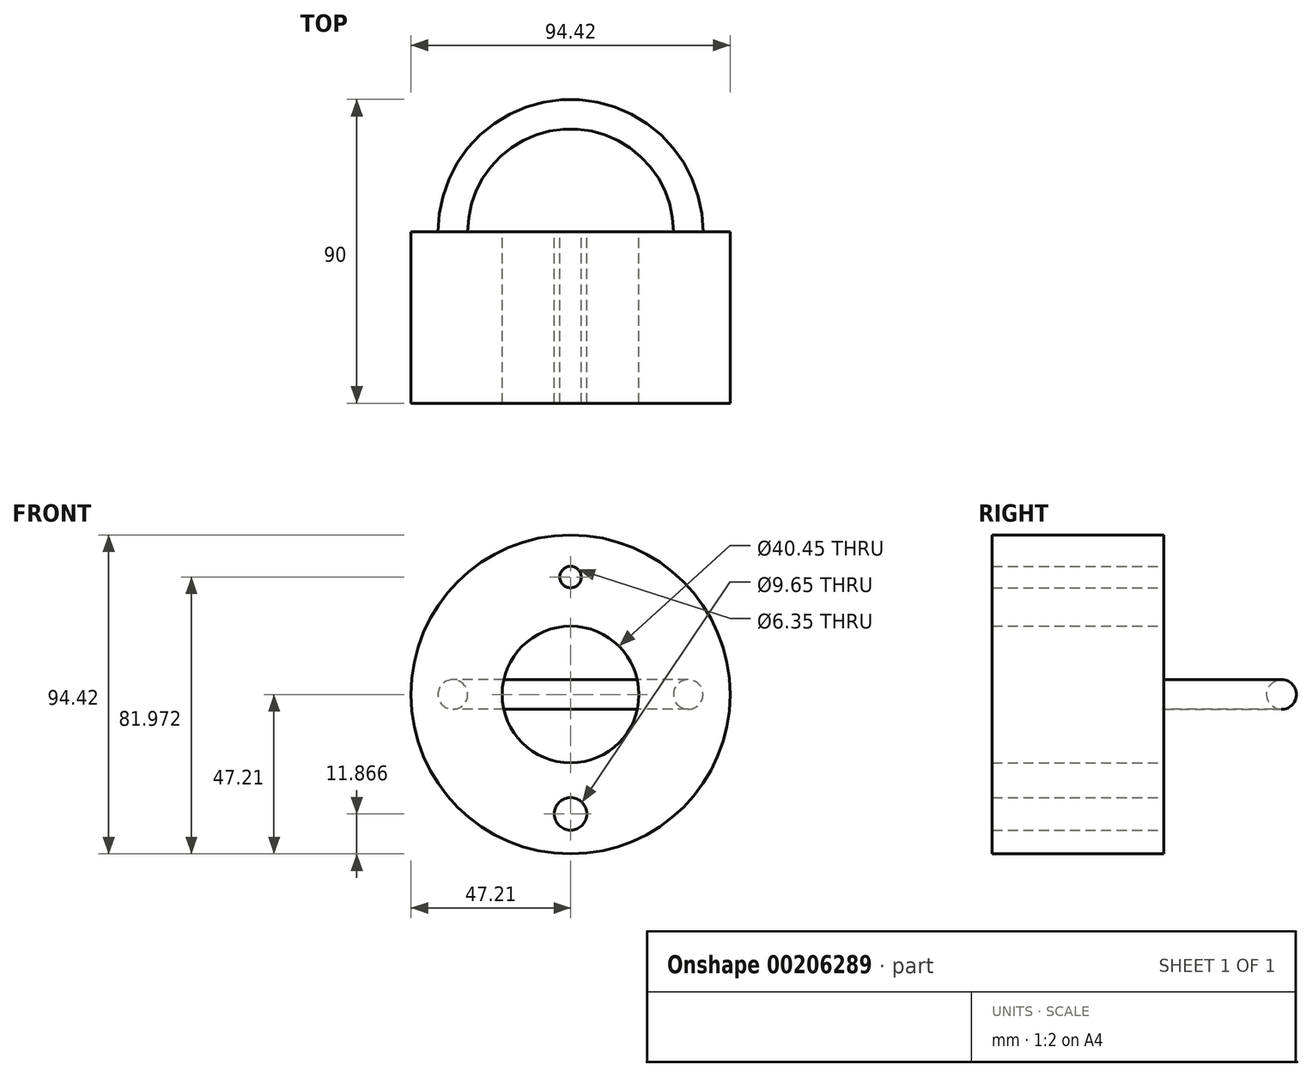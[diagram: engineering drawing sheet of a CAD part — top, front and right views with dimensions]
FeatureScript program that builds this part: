
annotation { "Feature Type Name" : "Feature", "Feature Type Description" : "" }
export const myFeature = defineFeature(function(context is Context, id is Id, definition is map)
    precondition{}
    {
        {
            var Q0;
            Q0=qCreatedBy(makeId("Front.planeOp"),FACE);
            var sketch = newSketch(context, id + "F0", { "sketchPlane" : qUnion([Q0])});
            skCircle(sketch, "E0", {"center": v(0, 0) * mm, "radius": 47.21 * mm});
            skCircle(sketch, "E1", {"center": v(0, 0) * mm, "radius": 20.23 * mm});
            skSolve(sketch);
        }
        {
            var Q0;
            Q0=makeQuery(id+"F0.imprint","IMPRINT",FACE,{"disambiguationData":[TD([[makeQuery(id+"F0.imprint","IMPRINT",EDGE,{"derivedFrom":sQuery(id+"F0.wireOp",EDGE,"E0")}),1.0]])]});
            extrude(context, id + "F1", {"entities" : qUnion([Q0]), "depth" : 50.8 * mm});
        }
        {
            var Q0;
            Q0=qCreatedBy(makeId("Front.planeOp"),FACE);
            var sketch = newSketch(context, id + "F2", { "sketchPlane" : qUnion([Q0])});
            skCircle(sketch, "E2", {"center": v(0, 34.76) * mm, "radius": 3.18 * mm});
            skCircle(sketch, "E3", {"center": v(0, -35.34) * mm, "radius": 4.82 * mm});
            skSolve(sketch);
        }
        {
            var Q0;
            Q0 = qSketchRegion(id + "F2", true);
            extrude(context, id + "F3", {"entities" : qUnion([Q0]), "operationType" : NewBodyOperationType.REMOVE, "endBound" : BoundingType.THROUGH_ALL, "depth" : 50.8 * mm});
        }
        {
            var Q0;
            Q0=qCreatedBy(makeId("Front.planeOp"),FACE);
            var sketch = newSketch(context, id + "F4", { "sketchPlane" : qUnion([Q0])});
            skCircle(sketch, "E4", {"center": v(-34.81, 0) * mm, "radius": 4.38 * mm});
            skLineSegment(sketch, "E5", {"start": v(0, -9.9) * mm, "end": v(0, 13.03) * mm});
            skSolve(sketch);
        }
        {
            var Q0;
            Q0 = qSketchRegion(id + "F4", true);
            var Q1;
            Q1=sQuery(id+"F4.wireOp",EDGE,"E5");
            revolve(context, id + "F5", {"operationType" : NewBodyOperationType.ADD, "entities" : qUnion([Q0]), "axis" : qUnion([Q1]), "revolveType" : RevolveType.ONE_DIRECTION, "oppositeDirection" : true, "angle" : 180 * degree});
        }
        {
            var Q0;
            Q0=makeQuery(id+"F1.opExtrude","CAP_FACE",FACE,{"disambiguationData":[OSD([sQuery(id+"F0.wireOp",EDGE,"E0"),sQuery(id+"F0.wireOp",EDGE,"E1")])],"isStart":false});
            var sketch = newSketch(context, id + "F6", { "sketchPlane" : qUnion([Q0])});
            skCircle(sketch, "E6", {"center": v(-35.15, 0) * mm, "radius": 3.9 * mm});
            skLineSegment(sketch, "E7", {"start": v(0, 0) * mm, "end": v(0, 15.34) * mm});
            skLineSegment(sketch, "E8", {"start": v(0, 15.34) * mm, "end": v(0, -14.76) * mm});
            skSolve(sketch);
        }
        {
            var Q0;
            Q0=sQuery(id+"F6.wireOp",EDGE,"E6");
            var Q1;
            Q1=sQuery(id+"F6.wireOp",EDGE,"E8");
            revolve(context, id + "F7", {"bodyType" : ExtendedToolBodyType.SURFACE, "surfaceEntities" : qUnion([Q0]), "axis" : qUnion([Q1]), "revolveType" : RevolveType.FULL});
        }
    });
